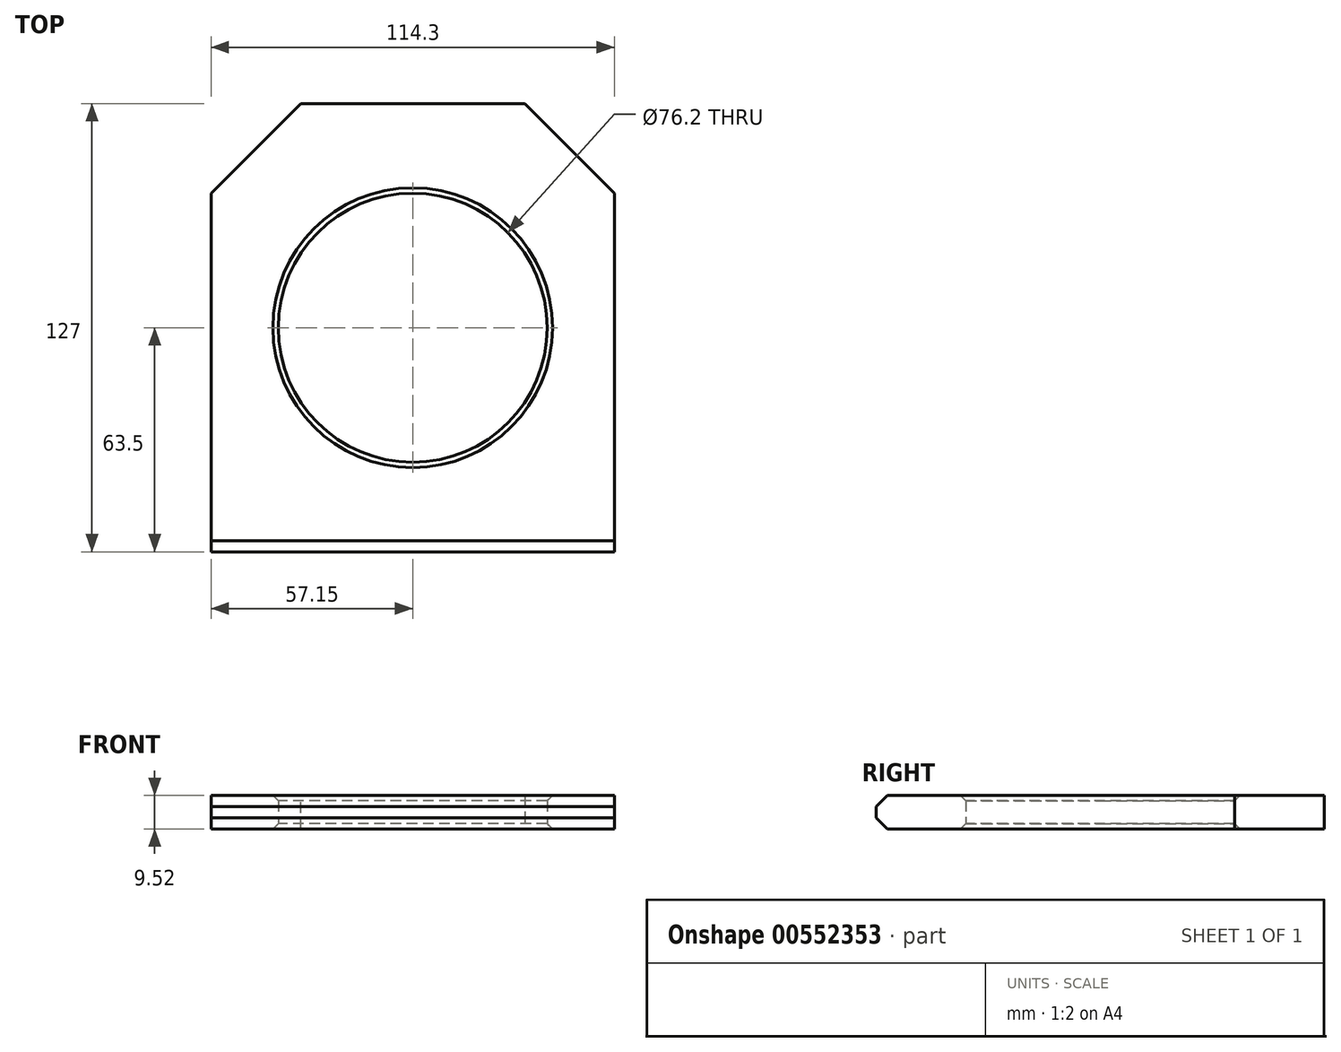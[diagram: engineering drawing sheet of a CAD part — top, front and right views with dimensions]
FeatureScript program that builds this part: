
annotation { "Feature Type Name" : "Feature", "Feature Type Description" : "" }
export const myFeature = defineFeature(function(context is Context, id is Id, definition is map)
    precondition{}
    {
        {
            var Q0;
            Q0=qCreatedBy(makeId("Top.planeOp"),FACE);
            var sketch = newSketch(context, id + "F0", { "sketchPlane" : qUnion([Q0]), "disableImprinting" : false});
            skLineSegment(sketch, "E0.bottom", {"start": v(57.15, -63.5) * mm, "end": v(-57.15, -63.5) * mm});
            skLineSegment(sketch, "E0.top", {"start": v(57.15, 63.5) * mm, "end": v(-57.15, 63.5) * mm});
            skLineSegment(sketch, "E0.left", {"start": v(57.15, -63.5) * mm, "end": v(57.15, 63.5) * mm});
            skLineSegment(sketch, "E0.right", {"start": v(-57.15, -63.5) * mm, "end": v(-57.15, 63.5) * mm});
            skPoint(sketch, "E0.middle", {"position": v(0, 0) * mm});
            skCircle(sketch, "E1", {"center": v(0, 0) * mm, "radius": 38.1 * mm});
            skSolve(sketch);
        }
        {
            var Q0;
            Q0=makeQuery(id+"F0.imprint","IMPRINT",FACE,{"disambiguationData":[TD([[makeQuery(id+"F0.imprint","IMPRINT",EDGE,{"derivedFrom":sQuery(id+"F0.wireOp",EDGE,"E0.bottom")}),-1.0]])]});
            extrude(context, id + "F1", {"entities" : qUnion([Q0]), "flatOperationType" : FlatOperationType.REMOVE, "depth" : 9.52 * mm, "offsetDistance" : 25.4 * mm, "symmetric" : true, "domain" : OperationDomain.MODEL});
        }
        {
            var Q0;
            Q0=makeQuery(id+"F1.opExtrude","SWEPT_EDGE",EDGE,{"disambiguationData":[OSD([sQuery(id+"F0.wireOp",EDGE,"E0.top"),sQuery(id+"F0.wireOp",EDGE,"E0.left")])]});
            var Q1;
            Q1=makeQuery(id+"F1.opExtrude","SWEPT_EDGE",EDGE,{"disambiguationData":[OSD([sQuery(id+"F0.wireOp",EDGE,"E0.top"),sQuery(id+"F0.wireOp",EDGE,"E0.right")])]});
            chamfer(context, id + "F2", {"entities" : qUnion([Q0, Q1]), "width" : 25.4 * mm, "tangentPropagation" : true});
        }
        {
            var Q0;
            Q0=makeQuery(id+"F1.opExtrude","CAP_EDGE",EDGE,{"disambiguationData":[OSD([sQuery(id+"F0.wireOp",EDGE,"E1")])],"isStart":false});
            var Q1;
            Q1=makeQuery(id+"F1.opExtrude","CAP_EDGE",EDGE,{"disambiguationData":[OSD([sQuery(id+"F0.wireOp",EDGE,"E1")])],"isStart":true});
            chamfer(context, id + "F3", {"entities" : qUnion([Q0, Q1]), "width" : 1.52 * mm, "tangentPropagation" : true});
        }
        {
            var Q0;
            Q0=makeQuery(id+"F1.opExtrude","CAP_EDGE",EDGE,{"disambiguationData":[OSD([sQuery(id+"F0.wireOp",EDGE,"E0.bottom")])],"isStart":false});
            var Q1;
            Q1=makeQuery(id+"F1.opExtrude","CAP_EDGE",EDGE,{"disambiguationData":[OSD([sQuery(id+"F0.wireOp",EDGE,"E0.bottom")])],"isStart":true});
            chamfer(context, id + "F4", {"entities" : qUnion([Q0, Q1]), "width" : 3.17 * mm, "tangentPropagation" : true});
        }
    });
